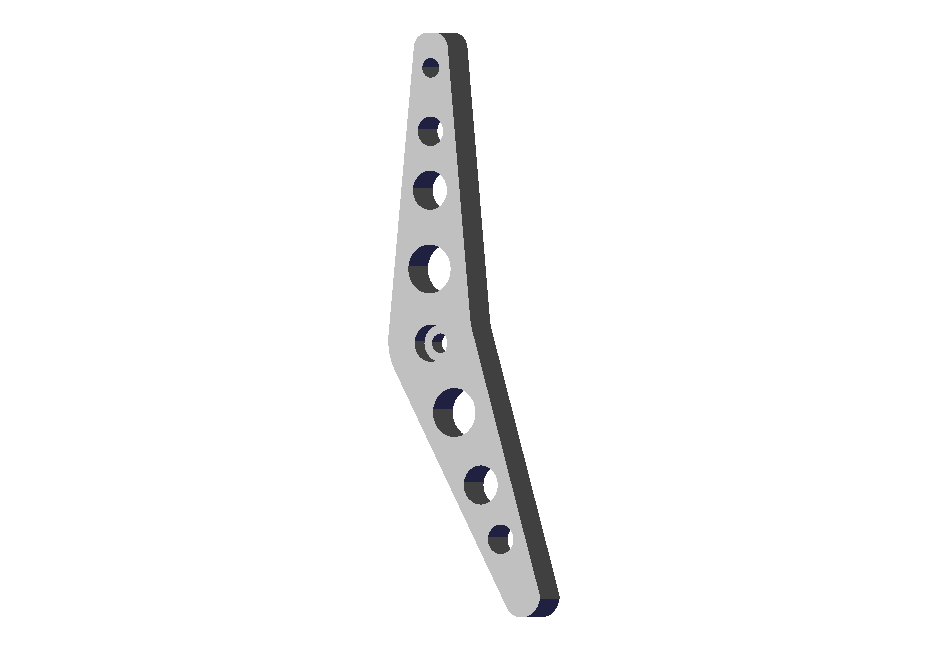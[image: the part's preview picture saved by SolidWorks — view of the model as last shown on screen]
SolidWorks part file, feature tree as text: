
SOLIDWORKS PART (.sldprt)
format: sldprt  version: not decoded by parser v0  size: 199,680 bytes
history: native  units: mm
features: extrude x32, sketch x5, cut_extrude x4, plane x3 (+5 scaffold rows collapsed)
feature tree (49):
  scaffold x5  (default folders/planes/origin — collapsed)
  plane  "Plane1"
  plane  "Plane2"
  plane  "Plane3"
  sketch  "Sketch1"  dims[c1.D8=8.0mm c1.D5=40.0mm c2.D8=10.0mm c2.D13=10.0mm c2.D2=30.0mm c2.D4=8.0mm c2.D5=8.0mm c2.D9=11.0mm c2.D1=~111.803399mm c3.D1=22.5deg c3.D2=10.0mm c3.D3=10.0mm c3.D4=10.0mm c3.D5=10.0mm c3.D6=150.0mm c3.D7=150.0mm c4.D6=150.0mm c4.D8=6.0mm c4.D9=6.0mm c4.D7=139.0mm c5.D8=~142.010876mm c5.D9=~145.989124mm c5.D10=150.0mm c5.D11=142.0mm c5.D5=10.0mm c6.D9=144.0mm c6.D12=~28.312243mm c6.D3=60.0mm c6.D6=20.0mm c6.D8=4.0mm c6.D11=~3.244752mm c7.D12=~2.98346mm c7.D13=~12.060308mm c7.D3=20.0mm c7.D11=5.0mm c8.D12=1.0mm c8.D13=60.0mm c8.D14=~60.087601mm c9.D13=145.0mm c9.D14=55.0mm c9.D15=2.0mm c9.D16=2.0mm c10.D13=53.0mm c10.D14=~4.582576mm c10.D17=150.0mm c11.D17=157.5deg c12.D17=~15.277013mm c12.D18=~146.717415mm]
  extrude  "Base-Extrude"  Depth=20mm cosForceComp:1=0
  extrude  "cosFMVItemName"  [1 undecoded]
  extrude  "cosForceRefPlaneName"  [1 undecoded]
  extrude  "cosFMVItemName"  [1 undecoded]
  sketch  "Sketch3"  dims[D1=10.0mm]
  cut_extrude  "Cut-Extrude2"  [1 undecoded]
  sketch  "Sketch4"  dims[c1.D3=10.0mm c1.D4=20.0mm c1.D5=20.0mm c1.D6=19.5375mm c2.D4=12.5mm c2.D5=15.625mm c2.D11=25.0mm c2.D9=10.0mm c2.D1=21.97mm c2.D3=25.0mm c3.D4=20.0mm c3.D5=15.0mm c3.D1=20.0mm c3.D2=5.0mm c3.D3=20.0mm c4.D4=8.0mm c4.D5=85.0mm c4.D6=35.0mm c4.D7=25.0mm c4.D8=20.0mm c4.D9=30.0mm c4.D10=31.25mm c5.D9=30.0mm c5.D1=~17.683607mm c5.D2=~30.818989mm c6.D1=~48.502597mm c6.D2=24.25mm c6.D6=30.0mm c6.D7=40.0mm c6.D8=~30.285995mm c7.D1=23.8mm c7.D2=~47.603327mm c7.D8=38.0mm c7.D9=38.0mm]
  cut_extrude  "Cut-Extrude3"  [1 undecoded]
  extrude  "cosForceRefPlaneName"  [1 undecoded]
  extrude  "cosFMVItemName"  [1 undecoded]
  extrude  "cosForceRefPlaneName"  [1 undecoded]
  extrude  "cosFMVItemName"  [1 undecoded]
  extrude  "cosForceRefPlaneName"  [1 undecoded]
  extrude  "cosFMVItemName"  [1 undecoded]
  sketch  "Sketch5"  dims[D1=10.0mm]
  cut_extrude  "Cut-Extrude4"  [1 undecoded]
  extrude  "sMaterialSourceName"  [1 undecoded]
  extrude  "sMaterialName"  [1 undecoded]
  extrude  "cosFMVItemName"  [1 undecoded]
  extrude  "cosMaterialName"  [1 undecoded]
  extrude  "cosComponentName"  Depth=0 cosMaterial4=0
  extrude  "sMaterialSourceName"  [1 undecoded]
  extrude  "sMaterialName"  [1 undecoded]
  extrude  "cosFMVItemName"  [1 undecoded]
  extrude  "cosMaterialName"  [1 undecoded]
  extrude  "cosComponentName"  Depth=0 cosFaceID=0
  extrude  "cosRestraintRefPlaneName"  [1 undecoded]
  extrude  "cosFMVItemName"  Depth=0 cosRestraint4=0
  extrude  "cosRestraintRefPlaneName"  [1 undecoded]
  extrude  "cosFMVItemName"  [1 undecoded]
  extrude  "cosRestraintRefPlaneName"  [1 undecoded]
  extrude  "cosFMVItemName"  [1 undecoded]
  extrude  "cosRestraintRefPlaneName"  [1 undecoded]
  extrude  "cosFMVItemName"  [1 undecoded]
  extrude  "cosRestraintRefPlaneName"  [1 undecoded]
  extrude  "cosFMVItemName"  [1 undecoded]
  extrude  "cosForceRefPlaneName"  [1 undecoded]
  extrude  "cosFMVItemName"  [1 undecoded]
  sketch  "Sketch6"  dims[D1=19.0mm]
  cut_extrude  "Cut-Extrude5"  Depth=10mm
decode coverage: 10 of 41 modeling features carry decoded parameters
note: ~ marks probable driven/reference dimensions
note: 31 parameter values undecoded
summary: no parameter record found for 31 features
note: suppression state not decoded; provenance and decode notes live in map.json
